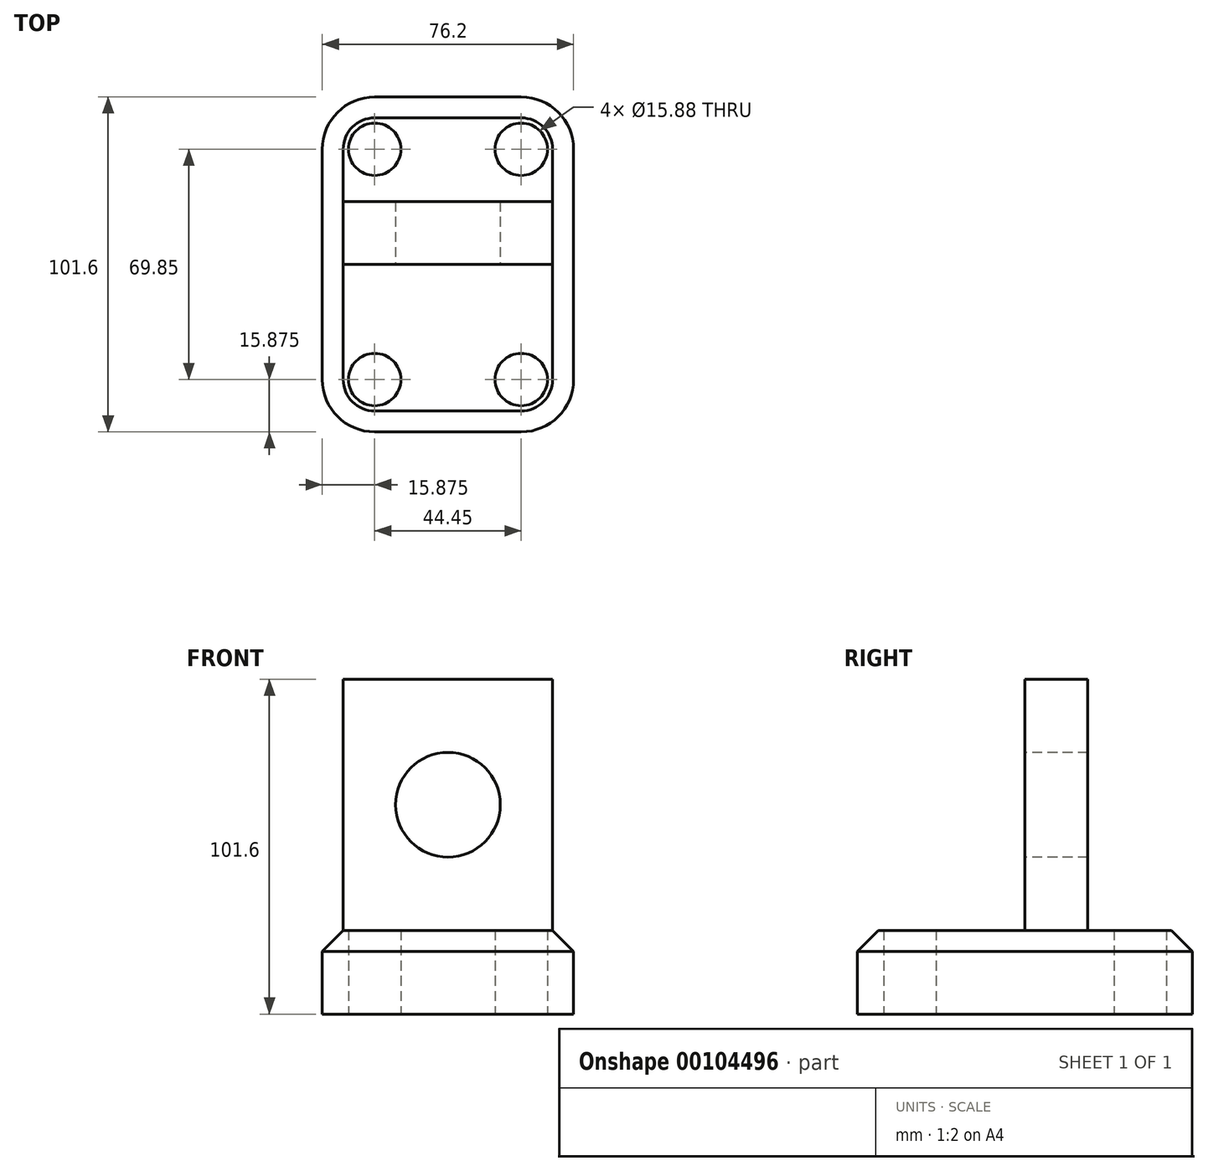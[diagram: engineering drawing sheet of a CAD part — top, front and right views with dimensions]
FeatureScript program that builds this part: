
annotation { "Feature Type Name" : "Feature", "Feature Type Description" : "" }
export const myFeature = defineFeature(function(context is Context, id is Id, definition is map)
    precondition{}
    {
        {
            var Q0;
            Q0=qCreatedBy(makeId("Top.planeOp"),FACE);
            var sketch = newSketch(context, id + "F0", { "sketchPlane" : qUnion([Q0])});
            skLineSegment(sketch, "E0.bottom", {"start": v(15.88, 0) * mm, "end": v(60.33, 0) * mm});
            skLineSegment(sketch, "E0.top", {"start": v(15.88, -101.6) * mm, "end": v(60.33, -101.6) * mm});
            skLineSegment(sketch, "E0.left", {"start": v(0, -15.88) * mm, "end": v(0, -85.72) * mm});
            skLineSegment(sketch, "E0.right", {"start": v(76.2, -15.88) * mm, "end": v(76.2, -85.72) * mm});
            skPoint(sketch, "E1.visualSharp", {"position": v(0, 0) * mm});
            skArc(sketch, "E1.filletArc", {"start": v(15.88, 0) * mm, "mid": v(4.65, -4.65) * mm, "end": v(0, -15.87) * mm});
            skPoint(sketch, "E2.visualSharp", {"position": v(76.2, 0) * mm});
            skArc(sketch, "E2.filletArc", {"start": v(76.2, -15.88) * mm, "mid": v(71.55, -4.65) * mm, "end": v(60.33, 0) * mm});
            skPoint(sketch, "E3.visualSharp", {"position": v(76.2, -101.6) * mm});
            skArc(sketch, "E3.filletArc", {"start": v(60.33, -101.6) * mm, "mid": v(71.55, -96.95) * mm, "end": v(76.2, -85.72) * mm});
            skPoint(sketch, "E4.visualSharp", {"position": v(0, -101.6) * mm});
            skArc(sketch, "E4.filletArc", {"start": v(0, -85.72) * mm, "mid": v(4.65, -96.95) * mm, "end": v(15.88, -101.6) * mm});
            skSolve(sketch);
        }
        {
            var Q0;
            Q0=makeQuery(id+"F0.imprint","IMPRINT",FACE,{"disambiguationData":[TD([[makeQuery(id+"F0.imprint","IMPRINT",EDGE,{"derivedFrom":sQuery(id+"F0.wireOp",EDGE,"E0.bottom")}),-1.0]])]});
            extrude(context, id + "F1", {"entities" : qUnion([Q0]), "depth" : 25.4 * mm});
        }
        {
            var Q0;
            Q0=sQuery(id+"F0.wireOp",VERTEX,"E1.filletArc.center");
            var Q1;
            Q1=sQuery(id+"F0.wireOp",VERTEX,"E2.filletArc.center");
            var Q2;
            Q2=sQuery(id+"F0.wireOp",VERTEX,"E3.filletArc.center");
            var Q3;
            Q3=sQuery(id+"F0.wireOp",VERTEX,"E4.filletArc.center");
            var Q4;
            Q4=makeQuery(id+"F1.opExtrude","SWEPT_BODY",BODY,{"disambiguationData":[OSD([sQuery(id+"F0.wireOp",EDGE,"E0.bottom"),sQuery(id+"F0.wireOp",EDGE,"E0.top"),sQuery(id+"F0.wireOp",EDGE,"E0.left"),sQuery(id+"F0.wireOp",EDGE,"E0.right"),sQuery(id+"F0.wireOp",EDGE,"E1.filletArc"),sQuery(id+"F0.wireOp",EDGE,"E2.filletArc"),sQuery(id+"F0.wireOp",EDGE,"E3.filletArc"),sQuery(id+"F0.wireOp",EDGE,"E4.filletArc")])]});
            hole(context, id + "F2", {"style" : HoleStyle.SIMPLE, "endStyle" : HoleEndStyle.THROUGH, "oppositeDirection" : true, "holeDiameter" : 15.88 * mm, "locations" : qUnion([Q0, Q1, Q2, Q3]), "scope" : qUnion([Q4]), "isTappedThrough" : true});
        }
        {
            var Q0;
            Q0=makeQuery(id+"F1.opExtrude","CAP_EDGE",EDGE,{"disambiguationData":[OSD([sQuery(id+"F0.wireOp",EDGE,"E1.filletArc")])],"isStart":false});
            chamfer(context, id + "F3", {"entities" : qUnion([Q0]), "width" : 6.35 * mm, "tangentPropagation" : true});
        }
        {
            var Q0;
            Q0=makeQuery(id+"F1.opExtrude","CAP_FACE",FACE,{"disambiguationData":[OSD([sQuery(id+"F0.wireOp",EDGE,"E0.bottom"),sQuery(id+"F0.wireOp",EDGE,"E0.top"),sQuery(id+"F0.wireOp",EDGE,"E0.left"),sQuery(id+"F0.wireOp",EDGE,"E0.right"),sQuery(id+"F0.wireOp",EDGE,"E1.filletArc"),sQuery(id+"F0.wireOp",EDGE,"E2.filletArc"),sQuery(id+"F0.wireOp",EDGE,"E3.filletArc"),sQuery(id+"F0.wireOp",EDGE,"E4.filletArc")])],"isStart":false});
            var sketch = newSketch(context, id + "F4", { "sketchPlane" : qUnion([Q0])});
            skLineSegment(sketch, "E5.bottom", {"start": v(0, 0) * mm, "end": v(6.35, 0) * mm});
            skLineSegment(sketch, "E5.top", {"start": v(0, -50.8) * mm, "end": v(6.35, -50.8) * mm});
            skLineSegment(sketch, "E5.left", {"start": v(0, 0) * mm, "end": v(0, -50.8) * mm});
            skLineSegment(sketch, "E5.right", {"start": v(6.35, 0) * mm, "end": v(6.35, -50.8) * mm});
            skLineSegment(sketch, "E6.bottom", {"start": v(6.35, -50.8) * mm, "end": v(69.85, -50.8) * mm});
            skLineSegment(sketch, "E6.top", {"start": v(6.35, -31.75) * mm, "end": v(69.85, -31.75) * mm});
            skLineSegment(sketch, "E6.left", {"start": v(6.35, -50.8) * mm, "end": v(6.35, -31.75) * mm});
            skLineSegment(sketch, "E6.right", {"start": v(69.85, -50.8) * mm, "end": v(69.85, -31.75) * mm});
            skSolve(sketch);
        }
        {
            var Q0;
            Q0=makeQuery(id+"F4.imprint","IMPRINT",FACE,{"disambiguationData":[TD([[makeQuery(id+"F4.imprint","IMPRINT",EDGE,{"derivedFrom":sQuery(id+"F4.wireOp",EDGE,"E6.bottom")}),1.0]])]});
            extrude(context, id + "F5", {"entities" : qUnion([Q0]), "operationType" : NewBodyOperationType.ADD, "depth" : 76.2 * mm});
        }
        {
            var Q0;
            Q0=makeQuery(id+"F5.opExtrude","SWEPT_FACE",FACE,{"disambiguationData":[OSD([sQuery(id+"F4.wireOp",EDGE,"E6.bottom")])]});
            var sketch = newSketch(context, id + "F6", { "sketchPlane" : qUnion([Q0])});
            skLineSegment(sketch, "E7", {"start": v(69.85, 25.4) * mm, "end": v(6.35, 25.4) * mm});
            skCircle(sketch, "E8", {"center": v(38.1, 63.5) * mm, "radius": 15.88 * mm});
            skPoint(sketch, "E9.start.orphan", {"position": v(6.35, 101.6) * mm});
            skLineSegment(sketch, "E10", {"start": v(22.23, 63.5) * mm, "end": v(22.23, 101.6) * mm});
            skLineSegment(sketch, "E11", {"start": v(22.23, 101.6) * mm, "end": v(22.23, 63.5) * mm});
            skLineSegment(sketch, "E12", {"start": v(53.98, 63.5) * mm, "end": v(53.97, 101.6) * mm});
            skPoint(sketch, "E13.start.orphan", {"position": v(69.85, 63.5) * mm});
            skPoint(sketch, "E14.start.orphan", {"position": v(6.35, 63.5) * mm});
            skSolve(sketch);
        }
        {
            var Q0;
            {var subQ0=sQuery(id+"F6.wireOp",EDGE,"E11");Q0=makeQuery(id+"F6.imprint","IMPRINT",FACE,{"disambiguationData":[TD([[makeQuery(id+"F6.imprint","IMPRINT",EDGE,{"derivedFrom":subQ0}),1.0]])]});}
            var Q1;
            {var subQ0=sQuery(id+"F6.wireOp",EDGE,"E8");var subQ1=makeQuery(id+"F6.imprint","INTERSECT",VERTEX,{"derivedFrom":[subQ0,sQuery(id+"F6.wireOp",EDGE,"E11")]});Q1=makeQuery(id+"F6.imprint","IMPRINT",FACE,{"disambiguationData":[TD([[makeQuery(id+"F6.imprint","IMPRINT",EDGE,{"disambiguationData":[TD([[subQ1,1.0]])],"derivedFrom":subQ0}),1.0]])]});}
            extrude(context, id + "F7", {"entities" : qUnion([Q0, Q1]), "operationType" : NewBodyOperationType.REMOVE, "oppositeDirection" : true, "depth" : 25.4 * mm});
        }
    });
